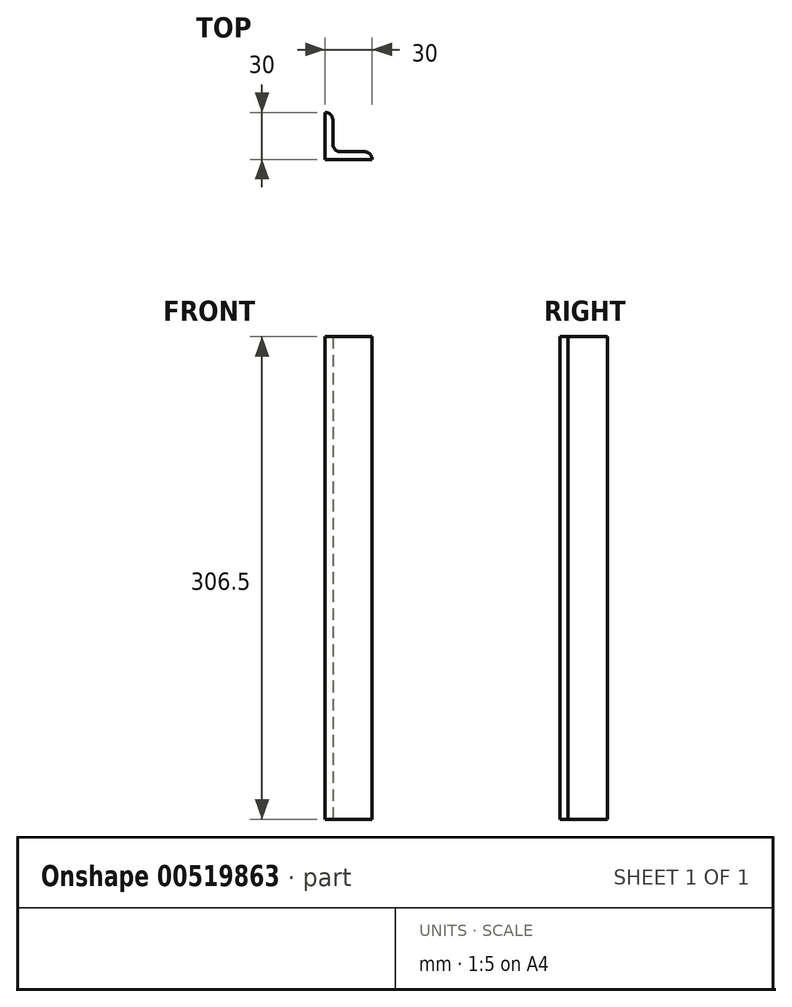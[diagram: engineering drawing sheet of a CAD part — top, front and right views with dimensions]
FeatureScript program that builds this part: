
annotation { "Feature Type Name" : "Feature", "Feature Type Description" : "" }
export const myFeature = defineFeature(function(context is Context, id is Id, definition is map)
    precondition{}
    {
        {
            var Q0;
            Q0=qCreatedBy(makeId("Top.planeOp"),FACE);
            var sketch = newSketch(context, id + "F0", { "sketchPlane" : qUnion([Q0])});
            skLineSegment(sketch, "E0", {"start": v(0, 0) * mm, "end": v(30, 0) * mm});
            skLineSegment(sketch, "E1", {"start": v(0, 0) * mm, "end": v(0, 30) * mm});
            skLineSegment(sketch, "E2", {"start": v(0, 30) * mm, "end": v(0, 30) * mm});
            skLineSegment(sketch, "E3", {"start": v(5, 25) * mm, "end": v(5, 10) * mm});
            skLineSegment(sketch, "E4", {"start": v(10, 5) * mm, "end": v(25, 5) * mm});
            skLineSegment(sketch, "E5", {"start": v(30, 0) * mm, "end": v(30, 0) * mm});
            skPoint(sketch, "E6.visualSharp", {"position": v(5, 5) * mm});
            skArc(sketch, "E6.filletArc", {"start": v(5, 10) * mm, "mid": v(6.46, 6.46) * mm, "end": v(10, 5) * mm});
            skPoint(sketch, "E7.visualSharp", {"position": v(5, 30) * mm});
            skArc(sketch, "E7.filletArc", {"start": v(5, 25) * mm, "mid": v(3.54, 28.54) * mm, "end": v(0, 30) * mm});
            skPoint(sketch, "E8.visualSharp", {"position": v(30, 5) * mm});
            skArc(sketch, "E8.filletArc", {"start": v(30, 0) * mm, "mid": v(28.54, 3.54) * mm, "end": v(25, 5) * mm});
            skSolve(sketch);
        }
        {
            var Q0;
            Q0 = qSketchRegion(id + "F0", true);
            extrude(context, id + "F1", {"entities" : qUnion([Q0]), "depth" : 306.5 * mm, "offsetDistance" : 25 * mm});
        }
    });
